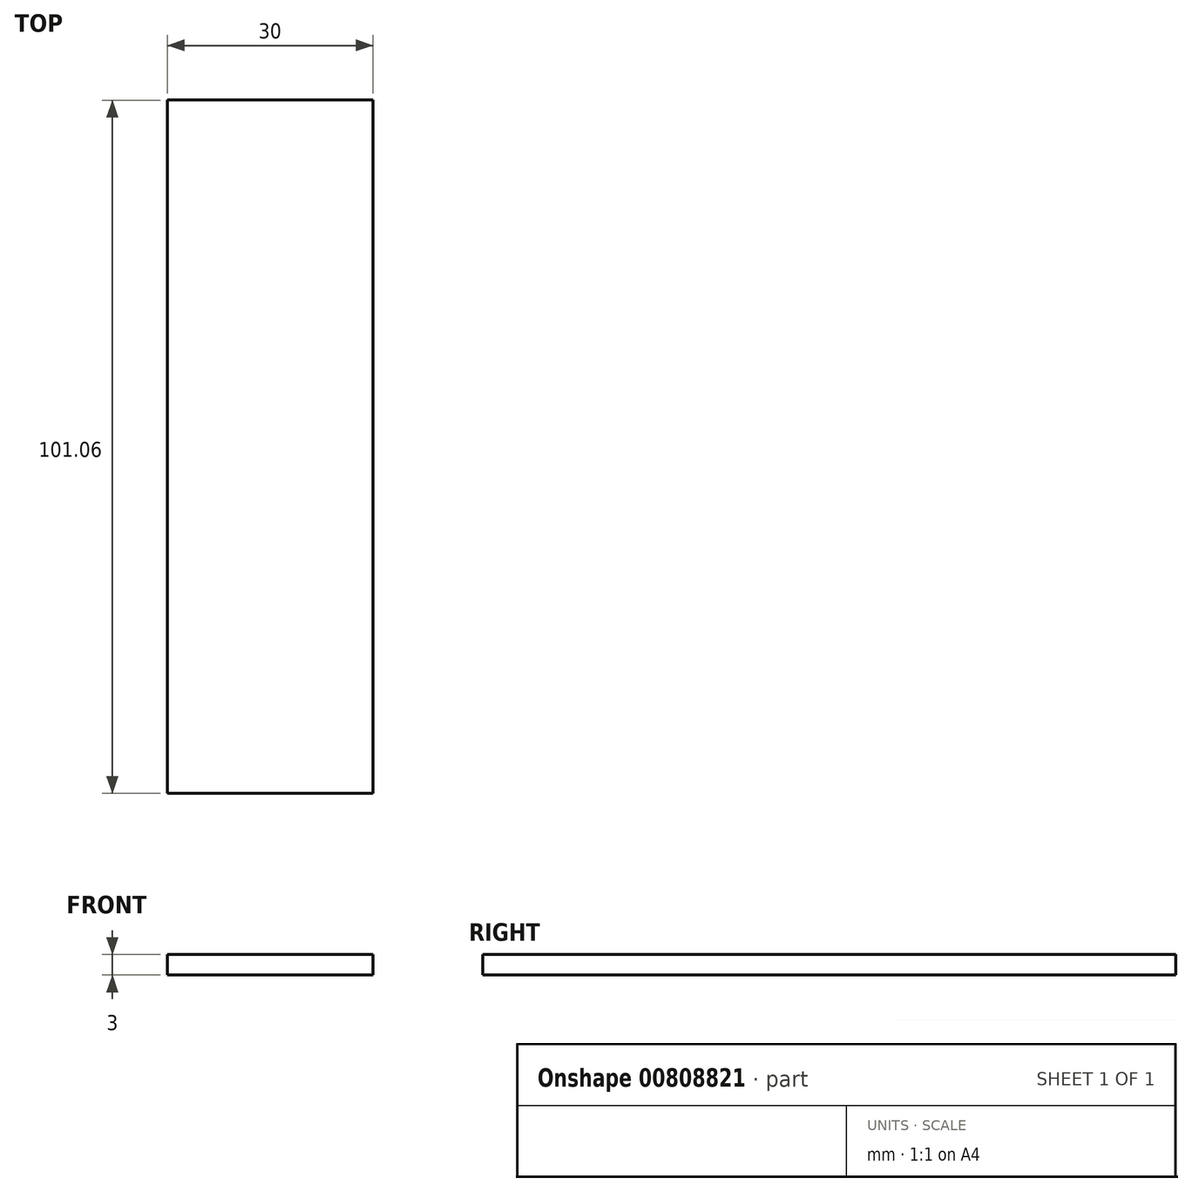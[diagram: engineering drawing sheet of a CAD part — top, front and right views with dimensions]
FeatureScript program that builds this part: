
annotation { "Feature Type Name" : "Feature", "Feature Type Description" : "" }
export const myFeature = defineFeature(function(context is Context, id is Id, definition is map)
    precondition{}
    {
        {
            var Q0;
            Q0=qCreatedBy(makeId("Top.planeOp"),FACE);
            var sketch = newSketch(context, id + "F0", { "sketchPlane" : qUnion([Q0])});
            skLineSegment(sketch, "E0.bottom", {"start": v(-15, 50.53) * mm, "end": v(15, 50.53) * mm});
            skLineSegment(sketch, "E0.top", {"start": v(-15, -50.53) * mm, "end": v(15, -50.53) * mm});
            skLineSegment(sketch, "E0.left", {"start": v(-15, 50.53) * mm, "end": v(-15, -50.53) * mm});
            skLineSegment(sketch, "E0.right", {"start": v(15, 50.53) * mm, "end": v(15, -50.53) * mm});
            skPoint(sketch, "E0.middle", {"position": v(0, 0) * mm});
            skSolve(sketch);
        }
        {
            var Q0;
            Q0=qSketchRegion(id+"F0",true);
            extrude(context, id + "F1", {"entities" : qUnion([Q0]), "depth" : 3 * mm, "offsetDistance" : 25 * mm});
        }
    });
